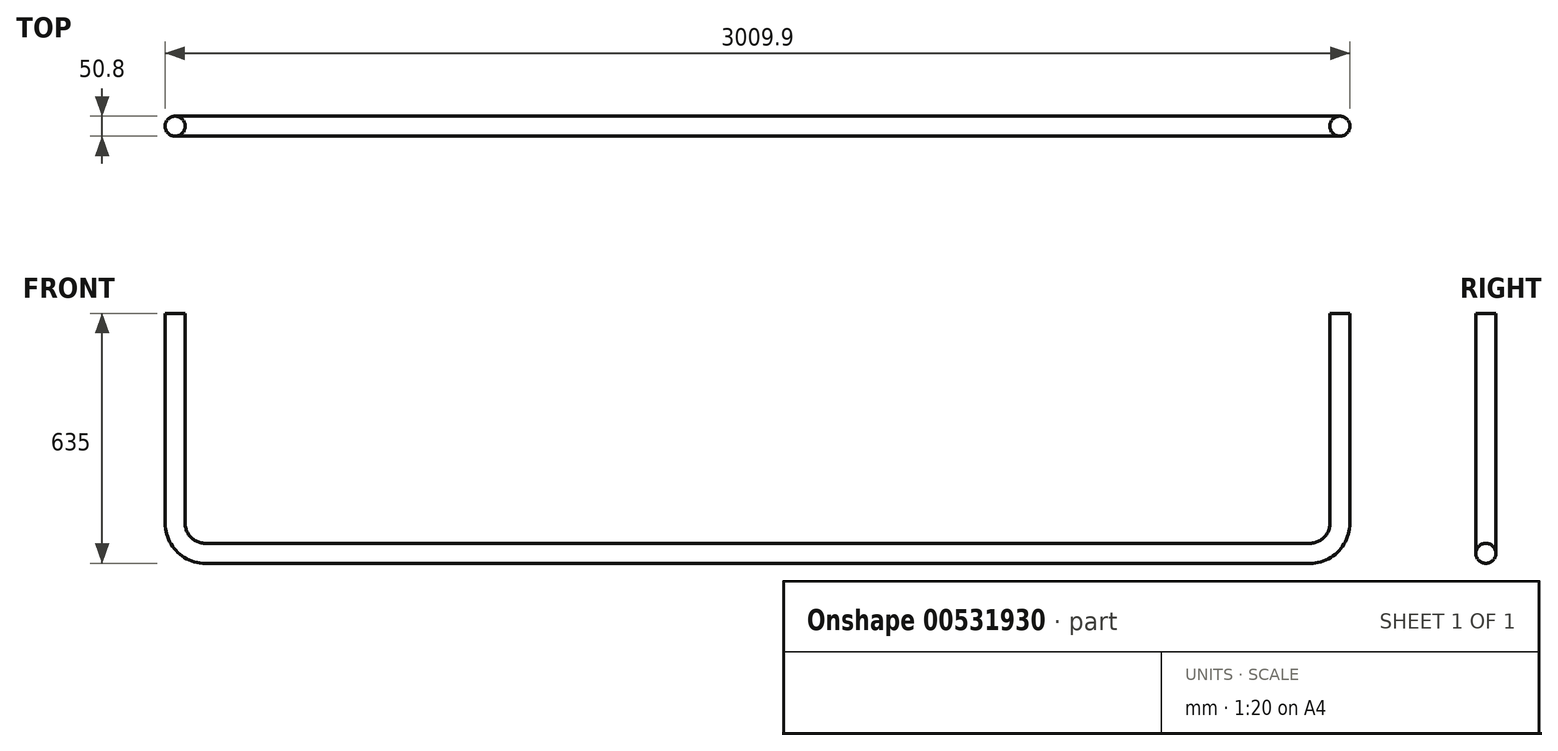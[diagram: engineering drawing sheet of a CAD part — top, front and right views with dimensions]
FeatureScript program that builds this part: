
annotation { "Feature Type Name" : "Feature", "Feature Type Description" : "" }
export const myFeature = defineFeature(function(context is Context, id is Id, definition is map)
    precondition{}
    {
        {
            var Q0;
            Q0=qCreatedBy(makeId("Front.planeOp"),FACE);
            var sketch = newSketch(context, id + "F0", { "sketchPlane" : qUnion([Q0])});
            skLineSegment(sketch, "E0", {"start": v(0, 0) * mm, "end": v(0, -533.4) * mm});
            skArc(sketch, "E1", {"start": v(0, -533.4) * mm, "mid": v(-22.32, -587.28) * mm, "end": v(-76.2, -609.6) * mm});
            skLineSegment(sketch, "E2", {"start": v(-76.2, -609.6) * mm, "end": v(-2882.9, -609.6) * mm});
            skArc(sketch, "E3", {"start": v(-2882.9, -609.6) * mm, "mid": v(-2936.78, -587.28) * mm, "end": v(-2959.1, -533.4) * mm});
            skLineSegment(sketch, "E4", {"start": v(-2959.1, -533.4) * mm, "end": v(-2959.1, 0) * mm});
            skSolve(sketch);
        }
        {
            var Q0;
            Q0=qCreatedBy(makeId("Top.planeOp"),FACE);
            var sketch = newSketch(context, id + "F1", { "sketchPlane" : qUnion([Q0])});
            skCircle(sketch, "E5", {"center": v(0, 0) * mm, "radius": 25.4 * mm});
            skSolve(sketch);
        }
        {
            var Q0;
            Q0=makeQuery(id+"F1.imprint","IMPRINT",FACE,{"disambiguationData":[TD([[makeQuery(id+"F1.imprint","IMPRINT",EDGE,{"derivedFrom":sQuery(id+"F1.wireOp",EDGE,"E5")}),1.0]])]});
            var Q1;
            Q1 = qConstructionFilter(qBodyType(qCreatedBy(id + "F0" ,EDGE), BodyType.WIRE), ConstructionObject.NO);
            sweep(context, id + "F2", {"profiles" : qUnion([Q0]), "path" : qUnion([Q1])});
        }
    });
